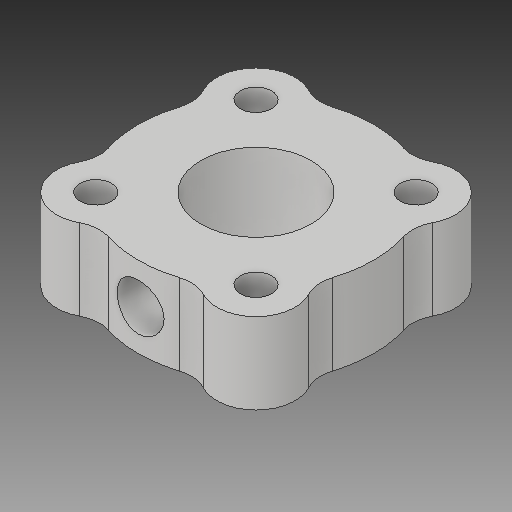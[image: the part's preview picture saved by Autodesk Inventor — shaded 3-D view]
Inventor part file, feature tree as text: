
AUTODESK INVENTOR PART (.ipt)
format: ipt  version: 2017 (Build 210142000, 142)  size: 151,040 bytes
history: native  units: in
note: dims shown in document units (in); Inventor stores cm internally (conversion verified against a paired STEP export)
features: fillet x1
ambient origin geometry x8: Origin, YZ Plane, XZ Plane, XY Plane, X Axis, Y Axis, Z Axis, Center Point
bodies: Solid1 (feature_tree)
feature tree (1):
  fillet  "Fillet1"  [1 undecoded]
note: 1 required parameter value undecoded (feature->parameter linkage not recoverable at this tier; creation-order binding heuristic only, values carry confidence <= 0.55)
